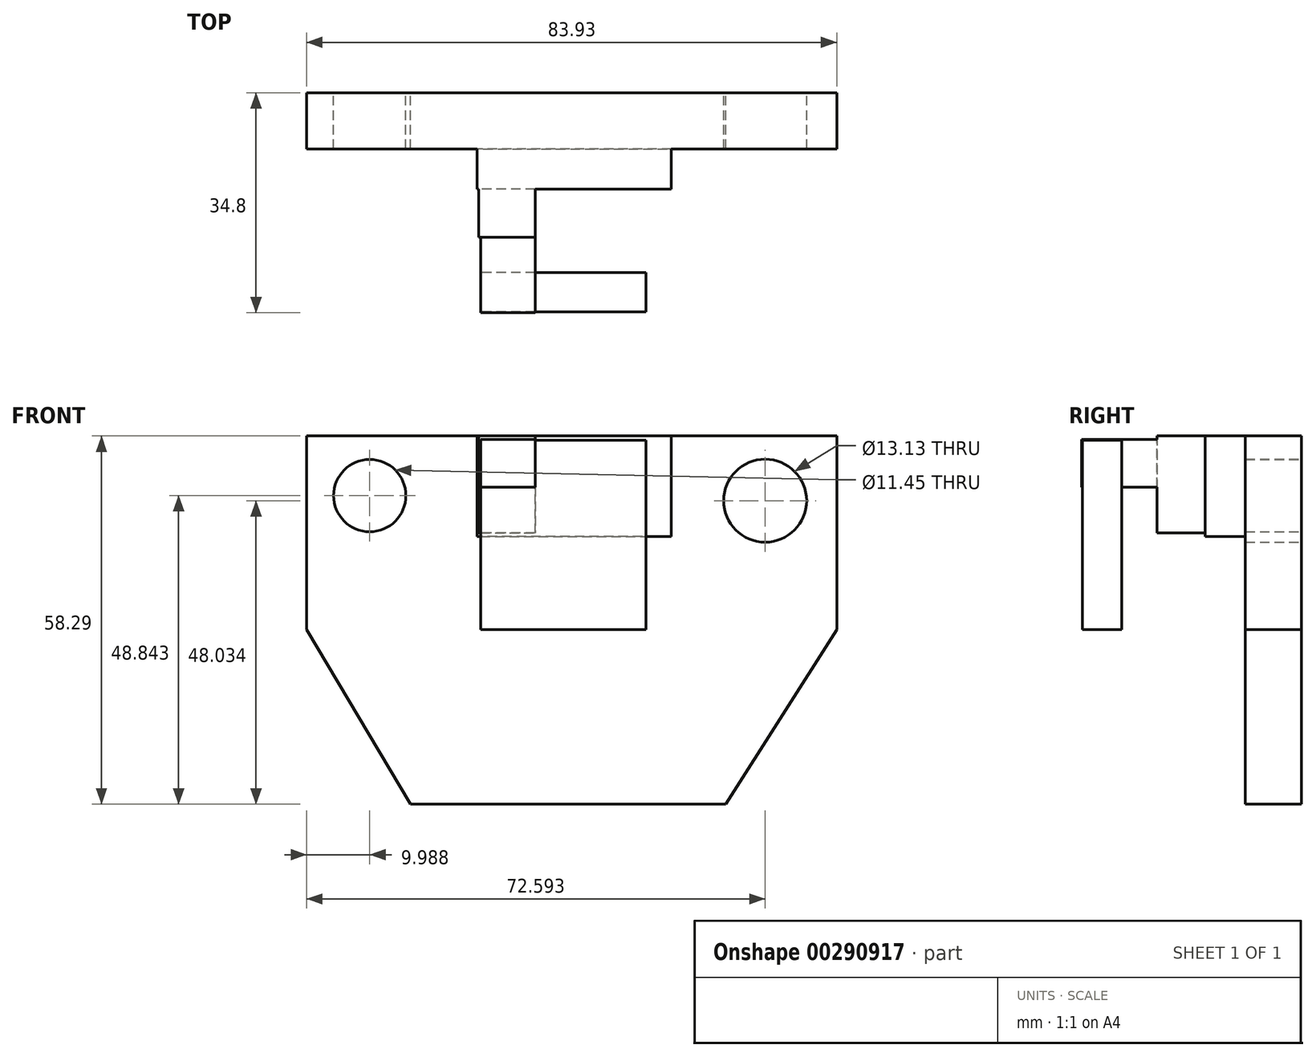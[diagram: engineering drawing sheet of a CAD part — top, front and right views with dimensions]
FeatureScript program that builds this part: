
annotation { "Feature Type Name" : "Feature", "Feature Type Description" : "" }
export const myFeature = defineFeature(function(context is Context, id is Id, definition is map)
    precondition{}
    {
        {
            var Q0;
            Q0=qCreatedBy(makeId("Front.planeOp"),FACE);
            var sketch = newSketch(context, id + "F0", { "sketchPlane" : qUnion([Q0])});
            skLineSegment(sketch, "E0.bottom", {"start": v(-42.9, 0) * mm, "end": v(41.02, 0) * mm});
            skLineSegment(sketch, "E0.top", {"start": v(-42.9, 30.63) * mm, "end": v(41.02, 30.63) * mm});
            skLineSegment(sketch, "E0.left", {"start": v(-42.9, 0) * mm, "end": v(-42.9, 30.63) * mm});
            skLineSegment(sketch, "E0.right", {"start": v(41.02, 0) * mm, "end": v(41.02, 30.63) * mm});
            skLineSegment(sketch, "E1", {"start": v(-42.9, 0) * mm, "end": v(-26.45, -27.66) * mm});
            skLineSegment(sketch, "E2", {"start": v(-26.45, -27.66) * mm, "end": v(23.48, -27.66) * mm});
            skLineSegment(sketch, "E3", {"start": v(23.48, -27.66) * mm, "end": v(41.02, 0) * mm});
            skSolve(sketch);
        }
        {
            var Q0;
            Q0 = qSketchRegion(id + "F0", true);
            extrude(context, id + "F1", {"entities" : qUnion([Q0]), "depth" : 8.9 * mm});
        }
        {
            var Q0;
            Q0=qCreatedBy(makeId("Front.planeOp"),FACE);
            var sketch = newSketch(context, id + "F2", { "sketchPlane" : qUnion([Q0])});
            skLineSegment(sketch, "E4.bottom", {"start": v(-15.92, 30.63) * mm, "end": v(14.84, 30.63) * mm});
            skLineSegment(sketch, "E4.top", {"start": v(-15.92, 14.7) * mm, "end": v(14.84, 14.7) * mm});
            skLineSegment(sketch, "E4.left", {"start": v(-15.92, 30.63) * mm, "end": v(-15.92, 14.7) * mm});
            skLineSegment(sketch, "E4.right", {"start": v(14.84, 30.63) * mm, "end": v(14.84, 14.7) * mm});
            skSolve(sketch);
        }
        {
            var Q0;
            Q0 = qSketchRegion(id + "F2", true);
            extrude(context, id + "F3", {"entities" : qUnion([Q0]), "operationType" : NewBodyOperationType.ADD, "depth" : 15.24 * mm});
        }
        {
            var Q0;
            Q0=qCreatedBy(makeId("Front.planeOp"),FACE);
            var sketch = newSketch(context, id + "F4", { "sketchPlane" : qUnion([Q0])});
            skLineSegment(sketch, "E5.bottom", {"start": v(-15.65, 30.63) * mm, "end": v(-6.75, 30.63) * mm});
            skLineSegment(sketch, "E5.top", {"start": v(-15.65, 15.25) * mm, "end": v(-6.75, 15.25) * mm});
            skLineSegment(sketch, "E5.left", {"start": v(-15.65, 30.63) * mm, "end": v(-15.65, 15.25) * mm});
            skLineSegment(sketch, "E5.right", {"start": v(-6.75, 30.63) * mm, "end": v(-6.75, 15.25) * mm});
            skSolve(sketch);
        }
        {
            var Q0;
            Q0 = qSketchRegion(id + "F4", true);
            extrude(context, id + "F5", {"entities" : qUnion([Q0]), "operationType" : NewBodyOperationType.ADD, "depth" : 22.86 * mm});
        }
        {
            var Q0;
            Q0=qCreatedBy(makeId("Front.planeOp"),FACE);
            var sketch = newSketch(context, id + "F6", { "sketchPlane" : qUnion([Q0])});
            skLineSegment(sketch, "E6.bottom", {"start": v(-15.38, 30.09) * mm, "end": v(-6.75, 30.09) * mm});
            skLineSegment(sketch, "E6.top", {"start": v(-15.38, 22.53) * mm, "end": v(-6.75, 22.53) * mm});
            skLineSegment(sketch, "E6.left", {"start": v(-15.38, 30.09) * mm, "end": v(-15.38, 22.53) * mm});
            skLineSegment(sketch, "E6.right", {"start": v(-6.75, 30.09) * mm, "end": v(-6.75, 22.53) * mm});
            skSolve(sketch);
        }
        {
            var Q0;
            Q0 = qSketchRegion(id + "F6", true);
            extrude(context, id + "F7", {"entities" : qUnion([Q0]), "operationType" : NewBodyOperationType.ADD, "depth" : 34.8 * mm});
        }
        {
            var Q0;
            Q0=qCreatedBy(makeId("Top.planeOp"),FACE);
            var sketch = newSketch(context, id + "F8", { "sketchPlane" : qUnion([Q0])});
            skLineSegment(sketch, "E7.bottom", {"start": v(-15.38, -34.68) * mm, "end": v(10.8, -34.68) * mm});
            skLineSegment(sketch, "E7.top", {"start": v(-15.38, -28.47) * mm, "end": v(10.8, -28.47) * mm});
            skLineSegment(sketch, "E7.left", {"start": v(-15.38, -34.68) * mm, "end": v(-15.38, -28.47) * mm});
            skLineSegment(sketch, "E7.right", {"start": v(10.8, -34.68) * mm, "end": v(10.8, -28.47) * mm});
            skSolve(sketch);
        }
        {
            var Q0;
            Q0 = qSketchRegion(id + "F8", true);
            extrude(context, id + "F9", {"entities" : qUnion([Q0]), "operationType" : NewBodyOperationType.ADD, "depth" : 29.97 * mm});
        }
        {
            var Q0;
            Q0=qCreatedBy(makeId("Front.planeOp"),FACE);
            var sketch = newSketch(context, id + "F10", { "sketchPlane" : qUnion([Q0])});
            skCircle(sketch, "E8", {"center": v(-32.92, 21.18) * mm, "radius": 5.72 * mm});
            skCircle(sketch, "E9", {"center": v(29.68, 20.37) * mm, "radius": 6.57 * mm});
            skSolve(sketch);
        }
        {
            var Q0;
            Q0 = qSketchRegion(id + "F10", true);
            extrude(context, id + "F11", {"entities" : qUnion([Q0]), "operationType" : NewBodyOperationType.REMOVE, "depth" : 25.4 * mm});
        }
    });
